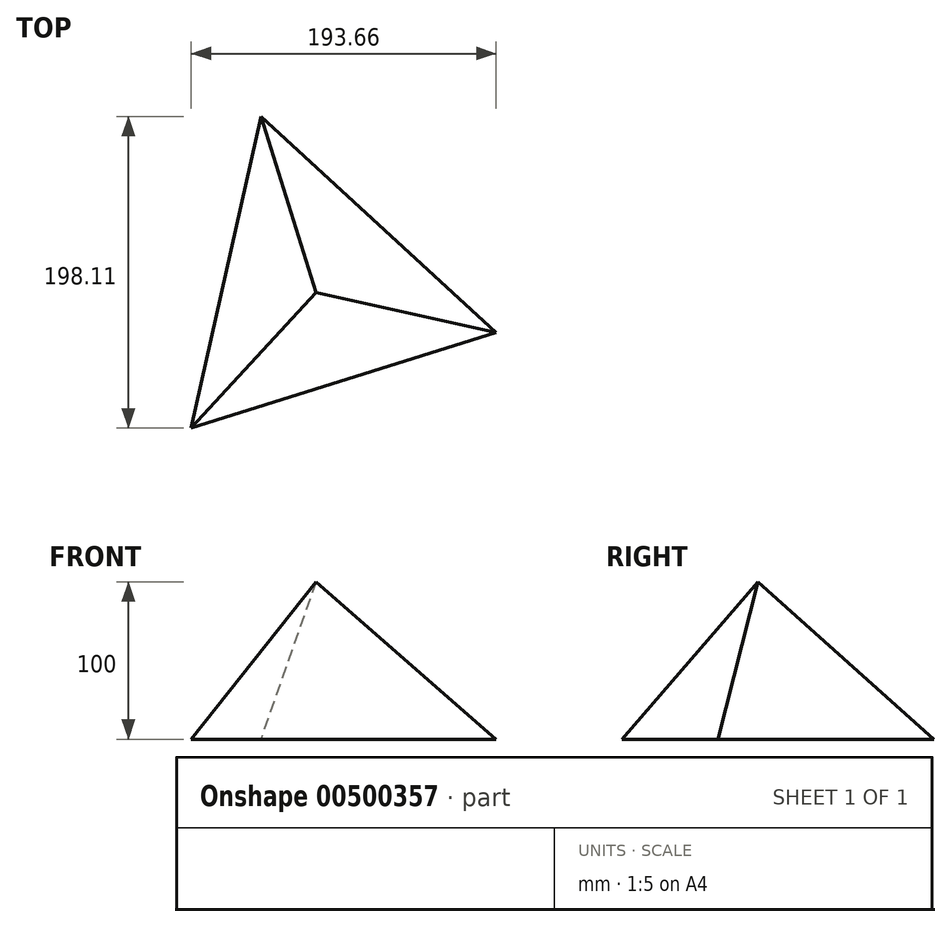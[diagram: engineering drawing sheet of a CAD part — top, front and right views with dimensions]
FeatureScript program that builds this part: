
annotation { "Feature Type Name" : "Feature", "Feature Type Description" : "" }
export const myFeature = defineFeature(function(context is Context, id is Id, definition is map)
    precondition{}
    {
        {
            var Q0;
            Q0=qCreatedBy(makeId("Top.planeOp"),FACE);
            var sketch = newSketch(context, id + "F0", { "sketchPlane" : qUnion([Q0])});
            skCircle(sketch, "E0.cCircle", {"center": v(0, 0) * mm, "radius": 117.19 * mm, "construction": true});
            skLineSegment(sketch, "E0.0", {"start": v(114.38, -25.5) * mm, "end": v(-79.28, -86.3) * mm});
            skLineSegment(sketch, "E0.1", {"start": v(-79.28, -86.3) * mm, "end": v(-35.1, 111.8) * mm});
            skLineSegment(sketch, "E0.2", {"start": v(-35.1, 111.8) * mm, "end": v(114.38, -25.5) * mm});
            skSolve(sketch);
        }
        {
            var Q0;
            Q0=qCreatedBy(makeId("Top.planeOp"),FACE);
            cPlane(context, id + "F1", {"entities" : qUnion([Q0]), "cplaneType" : CPlaneType.OFFSET, "offset" : 100 * mm, "width" : 152.4 * mm, "height" : 152.4 * mm});
        }
        {
            var Q0;
            Q0=qCreatedBy(id+"F1.planeOp",FACE);
            var sketch = newSketch(context, id + "F2", { "sketchPlane" : qUnion([Q0])});
            skPoint(sketch, "E1", {"position": v(0, 0) * mm});
            skSolve(sketch);
        }
        {
            var Q0;
            Q0=sQuery(id+"F2.wireOp",VERTEX,"E1");
            var Q1;
            Q1=makeQuery(id+"F0.imprint","IMPRINT",FACE,{"disambiguationData":[TD([[makeQuery(id+"F0.imprint","IMPRINT",EDGE,{"derivedFrom":sQuery(id+"F0.wireOp",EDGE,"E0.0")}),-1.0]])]});
            loft(context, id + "F3", {"sheetProfilesArray" : [{ "sheetProfileEntities" : qUnion([Q0]) }, { "sheetProfileEntities" : qUnion([Q1]) }]});
        }
    });
